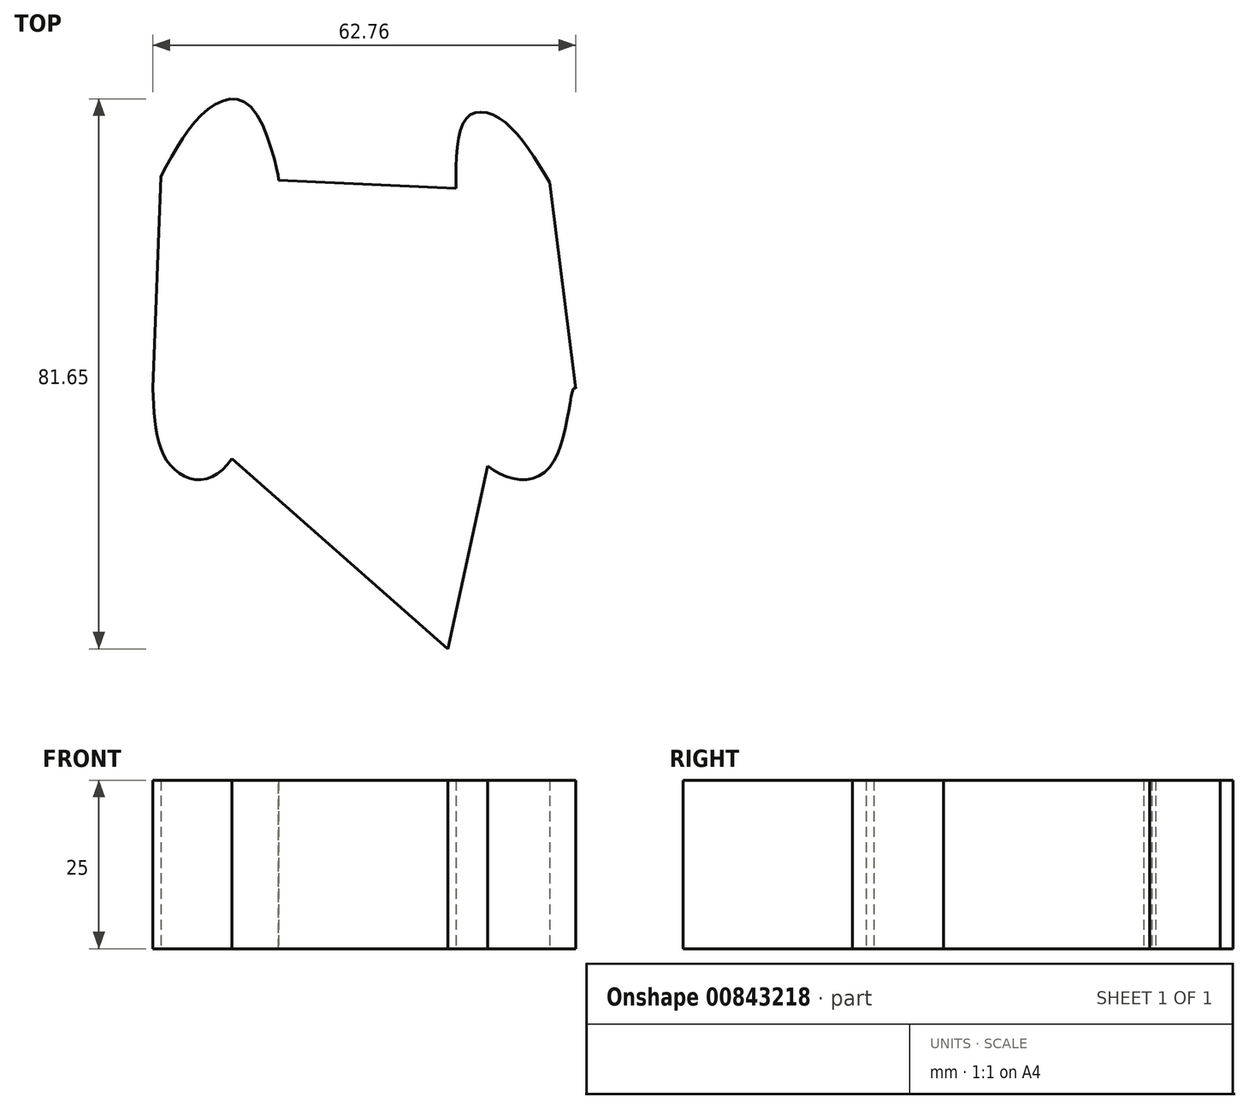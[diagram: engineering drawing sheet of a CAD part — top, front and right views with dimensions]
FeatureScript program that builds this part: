
annotation { "Feature Type Name" : "Feature", "Feature Type Description" : "" }
export const myFeature = defineFeature(function(context is Context, id is Id, definition is map)
    precondition{}
    {
        {
            var Q0;
            Q0=qCreatedBy(makeId("Top.planeOp"),FACE);
            var sketch = newSketch(context, id + "F0", { "sketchPlane" : qUnion([Q0])});
            skFitSpline(sketch, "E0", {"points": [v(-37.45, 31.53) * mm, v(-30.35, 41.6) * mm, v(-24.13, 41.9) * mm, v(-19.98, 31.23) * mm, v(-19.98, 30.94) * mm], "startDerivative": vector(18.13, 33.63) * mm, "endDerivative": vector(-0.64, -2.7) * mm});
            skFitSpline(sketch, "E1", {"points": [v(6.37, 29.75) * mm, v(8.14, 40.41) * mm, v(12.88, 40.12) * mm, v(20.28, 30.64) * mm], "startDerivative": vector(0.24, 37) * mm, "endDerivative": vector(18.03, -29.9) * mm});
            skFitSpline(sketch, "E2", {"points": [v(-38.63, 0) * mm, v(-36.27, -11.1) * mm, v(-30.05, -13.17) * mm, v(-21.76, 0) * mm], "startDerivative": vector(1.7, -37.43) * mm, "endDerivative": vector(18.56, 44.27) * mm});
            skFitSpline(sketch, "E3", {"points": [v(5.18, 0) * mm, v(11.4, -11.7) * mm, v(20.28, -11.7) * mm, v(23.83, 0) * mm, v(24.13, 0) * mm], "startDerivative": vector(12.82, -40.37) * mm, "endDerivative": vector(5.94, -3.35) * mm});
            skLineSegment(sketch, "E4", {"start": v(-19.98, 30.94) * mm, "end": v(6.37, 29.75) * mm});
            skLineSegment(sketch, "E5", {"start": v(-37.45, 31.53) * mm, "end": v(-38.63, 0) * mm});
            skLineSegment(sketch, "E6", {"start": v(-21.76, 0) * mm, "end": v(5.18, 0) * mm});
            skLineSegment(sketch, "E7", {"start": v(24.13, 0) * mm, "end": v(20.28, 30.64) * mm});
            skLineSegment(sketch, "E8", {"start": v(24.13, 0) * mm, "end": v(24.13, -38.63) * mm});
            skLineSegment(sketch, "E9", {"start": v(5.18, 0) * mm, "end": v(5.18, -38.63) * mm});
            skLineSegment(sketch, "E10", {"start": v(5.18, -38.63) * mm, "end": v(-21.76, 0) * mm});
            skLineSegment(sketch, "E11", {"start": v(-38.63, 0) * mm, "end": v(5.18, -38.63) * mm});
            skLineSegment(sketch, "E12", {"start": v(-19.97, 30.99) * mm, "end": v(5.18, -38.63) * mm});
            skLineSegment(sketch, "E13", {"start": v(-37.45, 31.53) * mm, "end": v(5.18, -38.63) * mm});
            skLineSegment(sketch, "E14", {"start": v(6.37, 29.75) * mm, "end": v(5.18, -38.63) * mm});
            skLineSegment(sketch, "E15", {"start": v(20.28, 30.64) * mm, "end": v(5.18, -38.63) * mm});
            skSolve(sketch);
        }
        {
            var Q0;
            Q0 = qSketchRegion(id + "F0", true);
            extrude(context, id + "F1", {"entities" : qUnion([Q0]), "depth" : 25 * mm, "offsetDistance" : 25 * mm});
        }
    });
